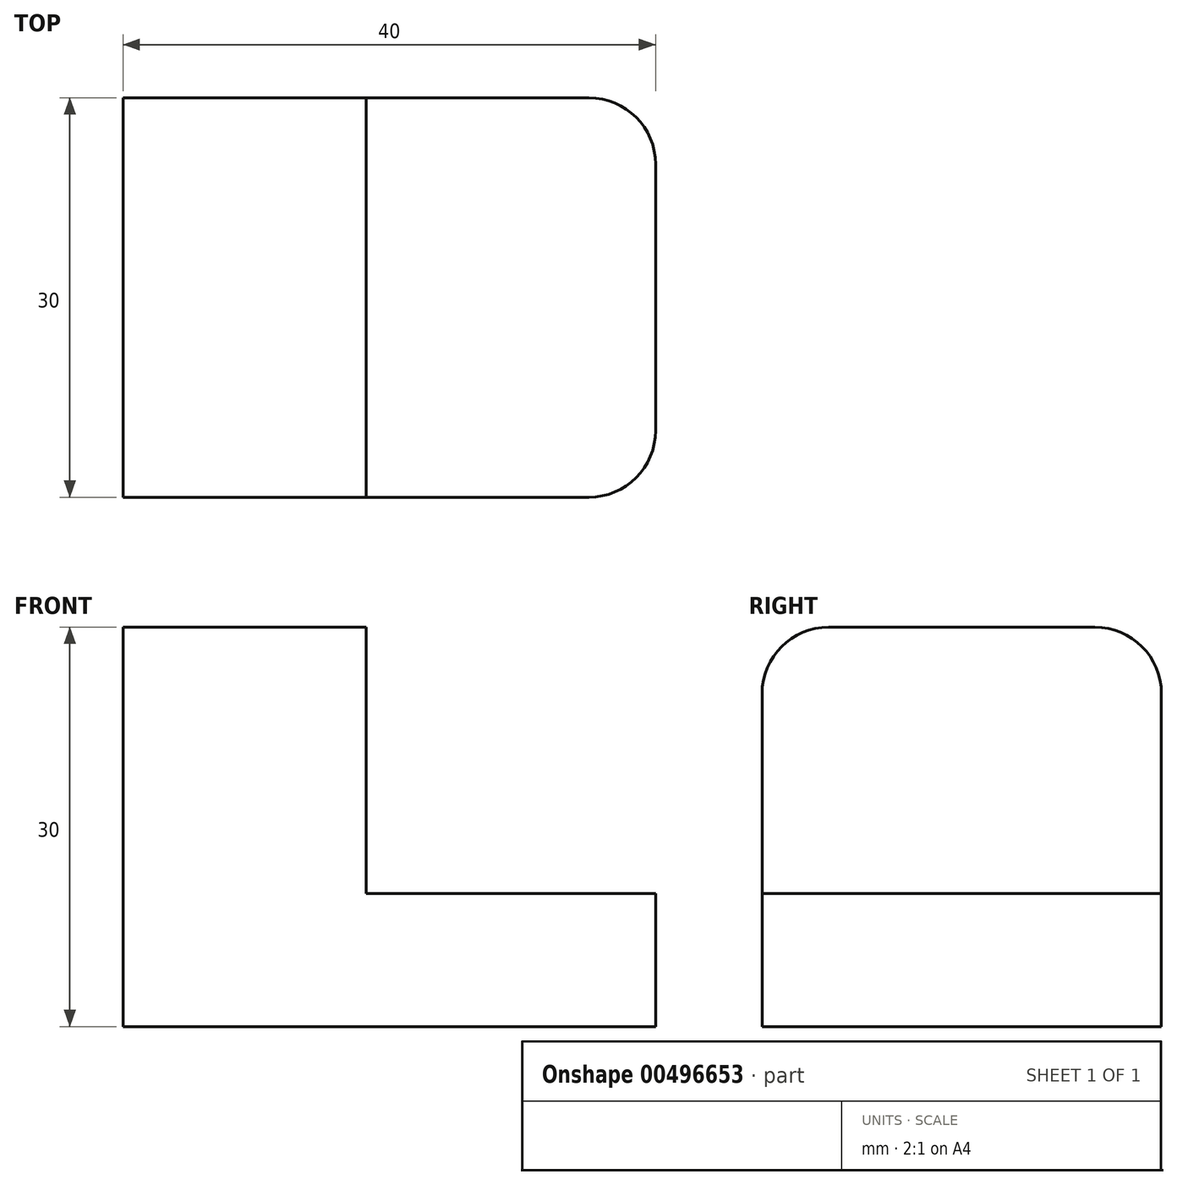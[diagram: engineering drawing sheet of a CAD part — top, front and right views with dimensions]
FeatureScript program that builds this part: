
annotation { "Feature Type Name" : "Feature", "Feature Type Description" : "" }
export const myFeature = defineFeature(function(context is Context, id is Id, definition is map)
    precondition{}
    {
        {
            var Q0;
            Q0=qCreatedBy(makeId("Front.planeOp"),FACE);
            var sketch = newSketch(context, id + "F0", { "sketchPlane" : qUnion([Q0])});
            skLineSegment(sketch, "E0", {"start": v(0, 0) * mm, "end": v(40, 0) * mm});
            skLineSegment(sketch, "E1", {"start": v(40, 0) * mm, "end": v(40, 10) * mm});
            skLineSegment(sketch, "E2", {"start": v(40, 10) * mm, "end": v(18.26, 10) * mm});
            skLineSegment(sketch, "E3", {"start": v(0, 0) * mm, "end": v(0, 30) * mm});
            skLineSegment(sketch, "E4", {"start": v(18.26, 10) * mm, "end": v(18.26, 20) * mm});
            skLineSegment(sketch, "E5", {"start": v(18.26, 20) * mm, "end": v(18.26, 30) * mm});
            skLineSegment(sketch, "E6", {"start": v(-1.74, 30) * mm, "end": v(18.26, 30) * mm});
            skLineSegment(sketch, "E7", {"start": v(32.5, 10) * mm, "end": v(32.5, 0) * mm});
            skLineSegment(sketch, "E8", {"start": v(0, 20) * mm, "end": v(18.26, 20) * mm});
            skLineSegment(sketch, "E9", {"start": v(0, 10) * mm, "end": v(18.26, 10) * mm});
            skSolve(sketch);
        }
        {
            var Q0;
            Q0 = qSketchRegion(id + "F0", true);
            extrude(context, id + "F1", {"entities" : qUnion([Q0]), "depth" : 30 * mm});
        }
        {
            var Q0;
            Q0=makeQuery(id+"F1.opExtrude","CAP_EDGE",EDGE,{"disambiguationData":[OSD([sQuery(id+"F0.wireOp",EDGE,"E6")])],"isStart":false});
            var Q1;
            Q1=makeQuery(id+"F1.opExtrude","CAP_EDGE",EDGE,{"disambiguationData":[OSD([sQuery(id+"F0.wireOp",EDGE,"E6")])],"isStart":true});
            var Q2;
            Q2=makeQuery(id+"F1.opExtrude","CAP_EDGE",EDGE,{"disambiguationData":[OSD([sQuery(id+"F0.wireOp",EDGE,"E1")])],"isStart":false});
            var Q3;
            Q3=makeQuery(id+"F1.opExtrude","CAP_EDGE",EDGE,{"disambiguationData":[OSD([sQuery(id+"F0.wireOp",EDGE,"E1")])],"isStart":true});
            fillet(context, id + "F2", {"entities" : qUnion([Q0, Q1, Q2, Q3]), "radius" : 5 * mm, "tangentPropagation" : true, "allowEdgeOverflow" : false});
        }
    });
